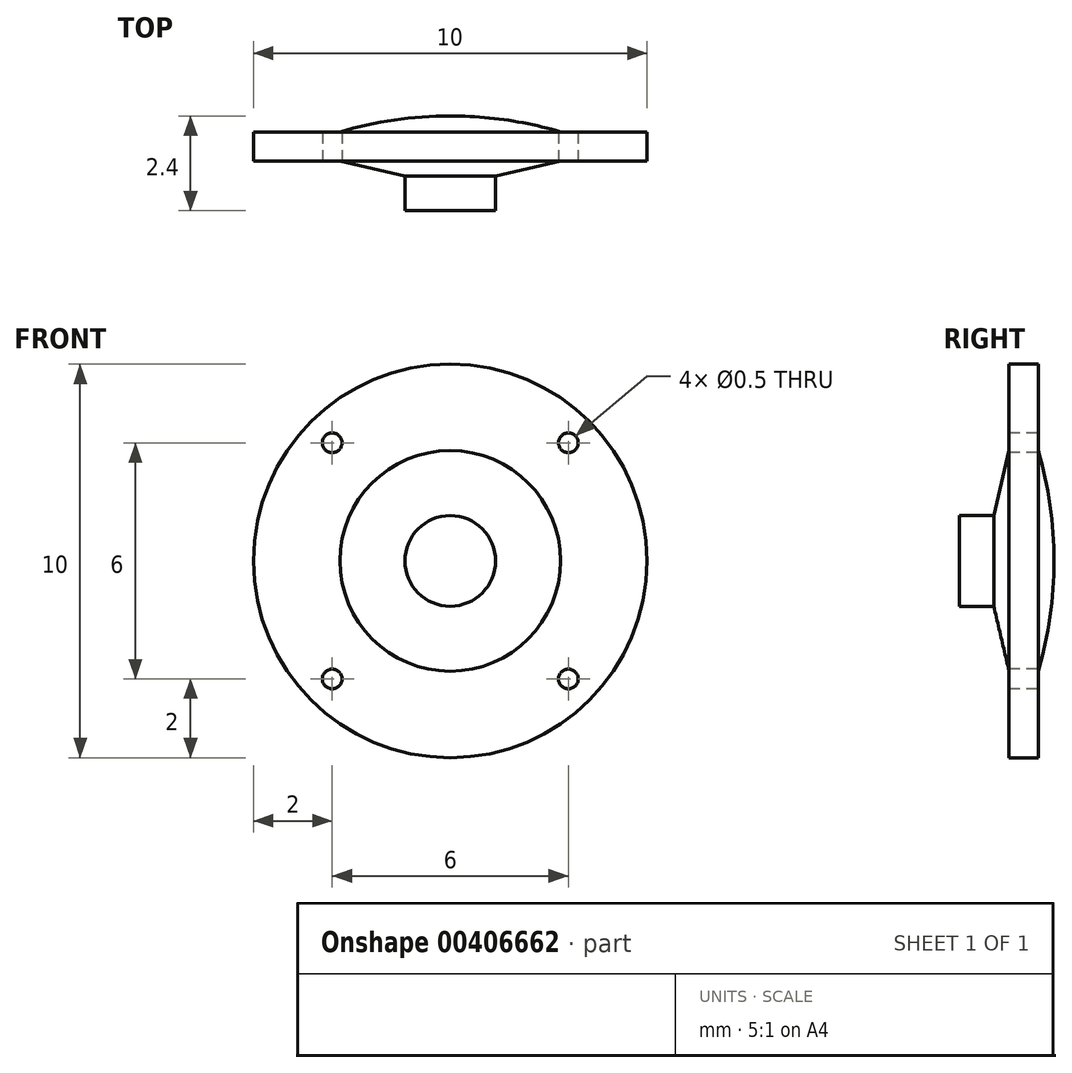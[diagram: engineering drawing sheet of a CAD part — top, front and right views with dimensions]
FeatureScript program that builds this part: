
annotation { "Feature Type Name" : "Feature", "Feature Type Description" : "" }
export const myFeature = defineFeature(function(context is Context, id is Id, definition is map)
    precondition{}
    {
        {
            var Q0;
            Q0=qCreatedBy(makeId("Top.planeOp"),FACE);
            var sketch = newSketch(context, id + "F0", { "sketchPlane" : qUnion([Q0])});
            skArc(sketch, "E0", {"start": v(0, 0.4) * mm, "mid": v(-1.42, 0.3) * mm, "end": v(-2.81, 0) * mm});
            skLineSegment(sketch, "E1", {"start": v(-2.81, 0) * mm, "end": v(-5, 0) * mm});
            skLineSegment(sketch, "E2", {"start": v(-5, 0) * mm, "end": v(-5, -0.74) * mm});
            skLineSegment(sketch, "E3", {"start": v(-5, -0.74) * mm, "end": v(-2.8, -0.74) * mm});
            skLineSegment(sketch, "E4", {"start": v(-2.8, -0.74) * mm, "end": v(-1.15, -1.13) * mm});
            skLineSegment(sketch, "E5", {"start": v(-1.15, -1.13) * mm, "end": v(-1.15, -2) * mm});
            skLineSegment(sketch, "E6", {"start": v(-1.15, -2) * mm, "end": v(0, -2) * mm});
            skLineSegment(sketch, "E7", {"start": v(0, -2) * mm, "end": v(0, 0.4) * mm});
            skPoint(sketch, "E8.orphan", {"position": v(2.81, 0) * mm});
            skSolve(sketch);
        }
        {
            var Q0;
            Q0=makeQuery(id+"F0.imprint","IMPRINT",FACE,{"disambiguationData":[TD([[makeQuery(id+"F0.imprint","IMPRINT",EDGE,{"derivedFrom":sQuery(id+"F0.wireOp",EDGE,"E0")}),1.0]])]});
            var Q1;
            Q1=sQuery(id+"F0.wireOp",EDGE,"E7");
            revolve(context, id + "F1", {"entities" : qUnion([Q0]), "axis" : qUnion([Q1]), "revolveType" : RevolveType.FULL});
        }
        {
            var Q0;
            Q0=makeQuery(id+"F1.opRevolve","SWEPT_FACE",FACE,{"disambiguationData":[OSD([sQuery(id+"F0.wireOp",EDGE,"E3")])]});
            var sketch = newSketch(context, id + "F2", { "sketchPlane" : qUnion([Q0])});
            skPoint(sketch, "E9.middle", {"position": v(0, 0) * mm});
            skCircle(sketch, "E10", {"center": v(3, 3) * mm, "radius": 0.25 * mm});
            skCircle(sketch, "E11", {"center": v(-3, 3) * mm, "radius": 0.25 * mm});
            skCircle(sketch, "E12", {"center": v(-3, -3) * mm, "radius": 0.25 * mm});
            skCircle(sketch, "E13", {"center": v(3, -3) * mm, "radius": 0.25 * mm});
            skSolve(sketch);
        }
        {
            var Q0;
            Q0 = qSketchRegion(id + "F2", true);
            extrude(context, id + "F3", {"entities" : qUnion([Q0]), "operationType" : NewBodyOperationType.REMOVE, "oppositeDirection" : true, "depth" : 25 * mm});
        }
    });
